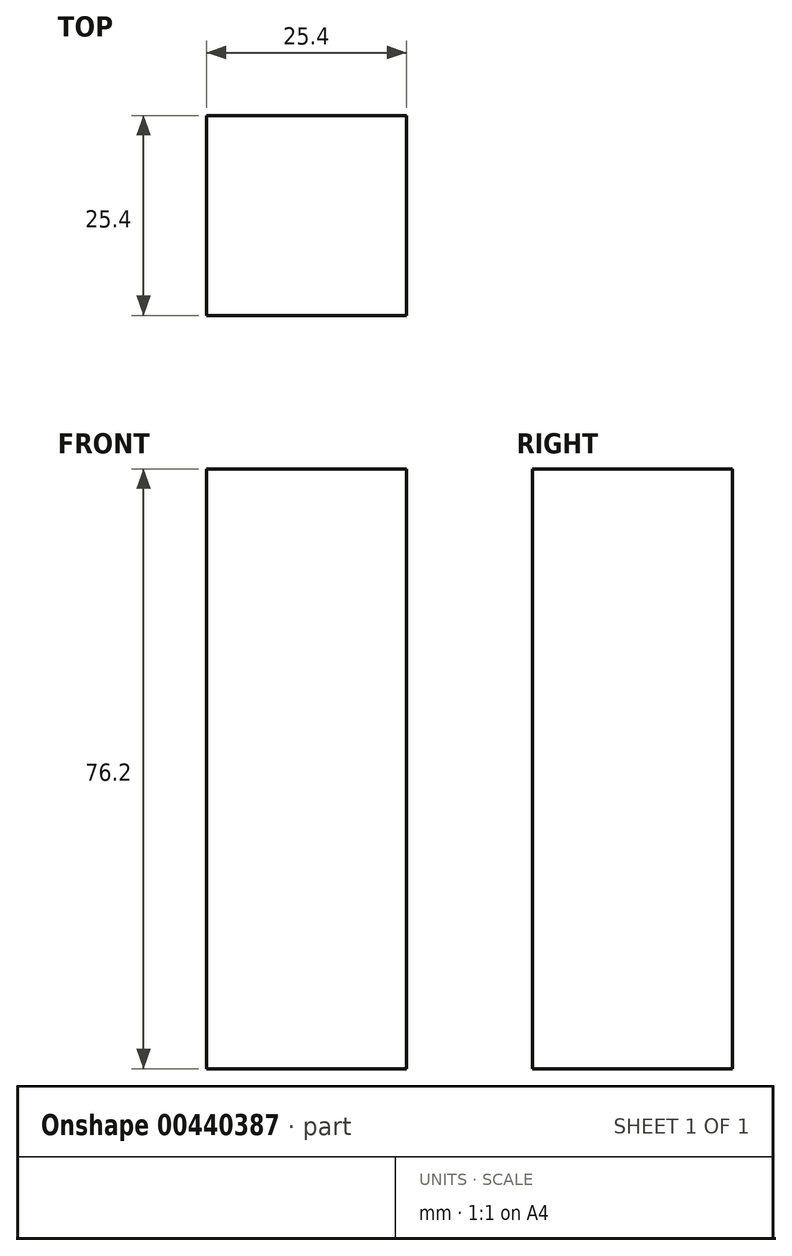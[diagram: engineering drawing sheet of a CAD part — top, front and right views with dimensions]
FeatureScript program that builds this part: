
annotation { "Feature Type Name" : "Feature", "Feature Type Description" : "" }
export const myFeature = defineFeature(function(context is Context, id is Id, definition is map)
    precondition{}
    {
        {
            var Q0;
            Q0=qCreatedBy(makeId("Top.planeOp"),FACE);
            var sketch = newSketch(context, id + "F0", { "sketchPlane" : qUnion([Q0])});
            skLineSegment(sketch, "E0.bottom", {"start": v(-47.36, 11.84) * mm, "end": v(-21.96, 11.84) * mm});
            skLineSegment(sketch, "E0.top", {"start": v(-47.36, 37.24) * mm, "end": v(-21.96, 37.24) * mm});
            skLineSegment(sketch, "E0.left", {"start": v(-47.36, 11.84) * mm, "end": v(-47.36, 37.24) * mm});
            skLineSegment(sketch, "E0.right", {"start": v(-21.96, 11.84) * mm, "end": v(-21.96, 37.24) * mm});
            skSolve(sketch);
        }
        {
            var Q0;
            Q0=makeQuery(id+"F0.imprint","IMPRINT",FACE,{"disambiguationData":[TD([[makeQuery(id+"F0.imprint","IMPRINT",EDGE,{"derivedFrom":sQuery(id+"F0.wireOp",EDGE,"E0.bottom")}),1.0]])]});
            extrude(context, id + "F1", {"entities" : qUnion([Q0]), "depth" : 76.2 * mm});
        }
    });
